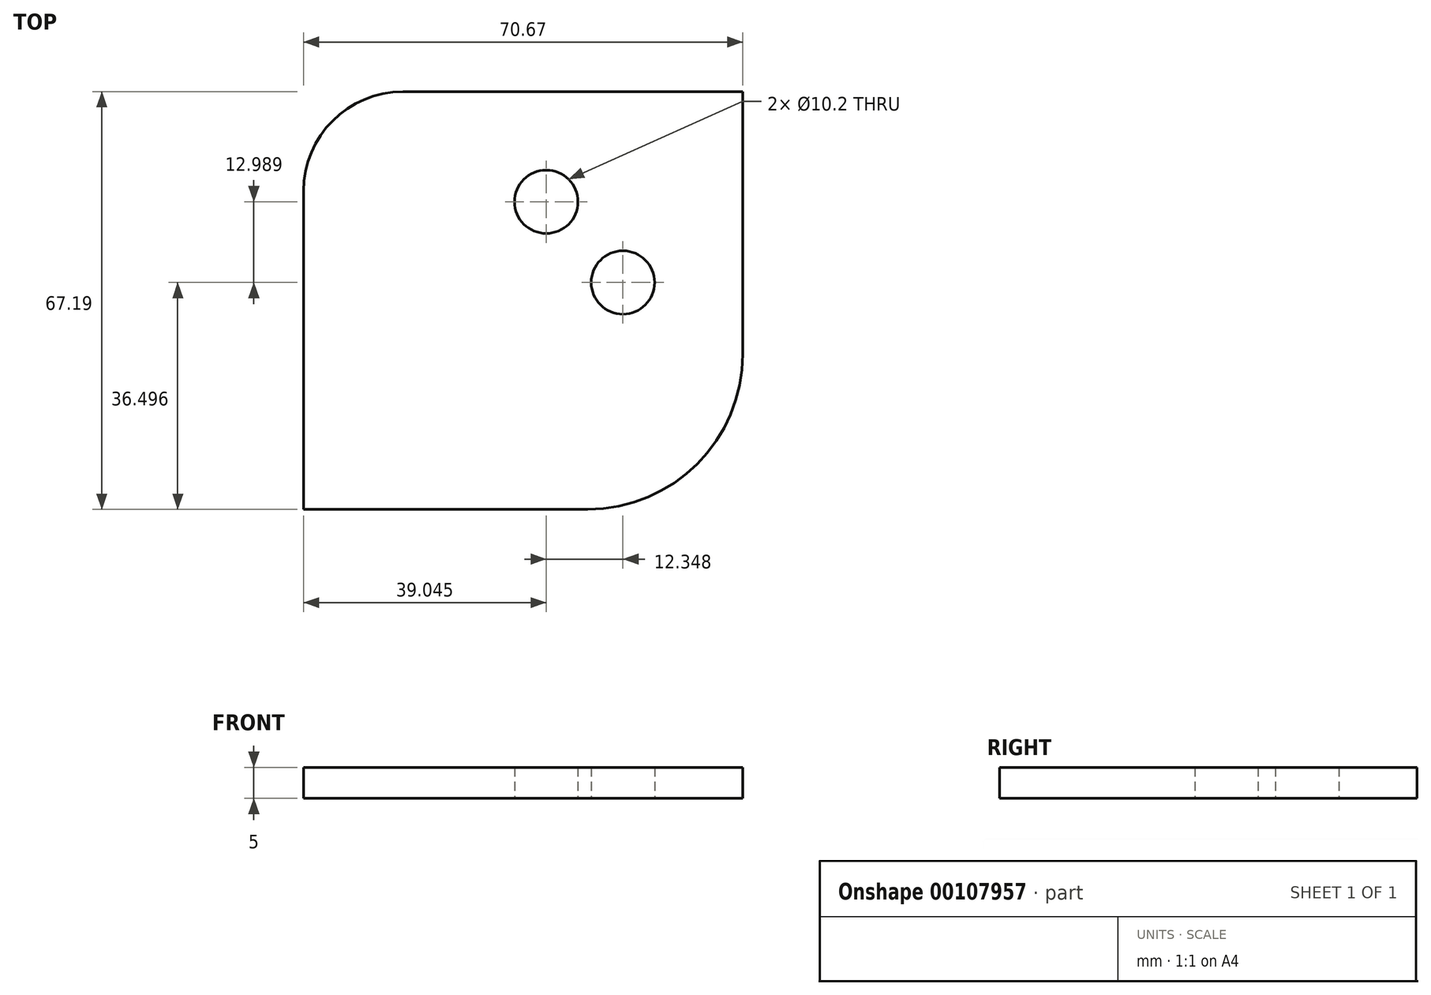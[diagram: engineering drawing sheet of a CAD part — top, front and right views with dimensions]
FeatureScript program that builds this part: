
annotation { "Feature Type Name" : "Feature", "Feature Type Description" : "" }
export const myFeature = defineFeature(function(context is Context, id is Id, definition is map)
    precondition{}
    {
        {
            var Q0;
            Q0=qCreatedBy(makeId("Top.planeOp"),FACE);
            var sketch = newSketch(context, id + "F0", { "sketchPlane" : qUnion([Q0])});
            skLineSegment(sketch, "E0.bottom", {"start": v(-16.89, 28.82) * mm, "end": v(37.81, 28.82) * mm});
            skLineSegment(sketch, "E0.top", {"start": v(-32.86, -38.37) * mm, "end": v(12.83, -38.37) * mm});
            skLineSegment(sketch, "E0.left", {"start": v(-32.86, 12.85) * mm, "end": v(-32.86, -38.37) * mm});
            skLineSegment(sketch, "E0.right", {"start": v(37.81, 28.82) * mm, "end": v(37.81, -13.38) * mm});
            skPoint(sketch, "E1.visualSharp", {"position": v(-32.86, 28.82) * mm});
            skArc(sketch, "E1.filletArc", {"start": v(-16.89, 28.82) * mm, "mid": v(-28.18, 24.14) * mm, "end": v(-32.86, 12.85) * mm});
            skPoint(sketch, "E2.visualSharp", {"position": v(37.81, -38.37) * mm});
            skArc(sketch, "E2.filletArc", {"start": v(12.83, -38.37) * mm, "mid": v(30.5, -31.05) * mm, "end": v(37.81, -13.38) * mm});
            skLineSegment(sketch, "E3", {"start": v(37.81, 28.82) * mm, "end": v(-32.86, -38.37) * mm});
            skCircle(sketch, "E4", {"center": v(6.18, 11.11) * mm, "radius": 5.1 * mm});
            skCircle(sketch, "E5.MirrorC", {"center": v(18.53, -1.87) * mm, "radius": 5.1 * mm});
            skSolve(sketch);
        }
        {
            var Q0;
            Q0=makeQuery(id+"F0.imprint","IMPRINT",FACE,{"disambiguationData":[TD([[makeQuery(id+"F0.imprint","IMPRINT",EDGE,{"derivedFrom":sQuery(id+"F0.wireOp",EDGE,"E0.bottom")}),-1.0]])]});
            var Q1;
            Q1=makeQuery(id+"F0.imprint","IMPRINT",FACE,{"disambiguationData":[TD([[makeQuery(id+"F0.imprint","IMPRINT",EDGE,{"derivedFrom":sQuery(id+"F0.wireOp",EDGE,"E0.top")}),1.0]])]});
            extrude(context, id + "F1", {"entities" : qUnion([Q0, Q1]), "depth" : 5 * mm});
        }
    });
